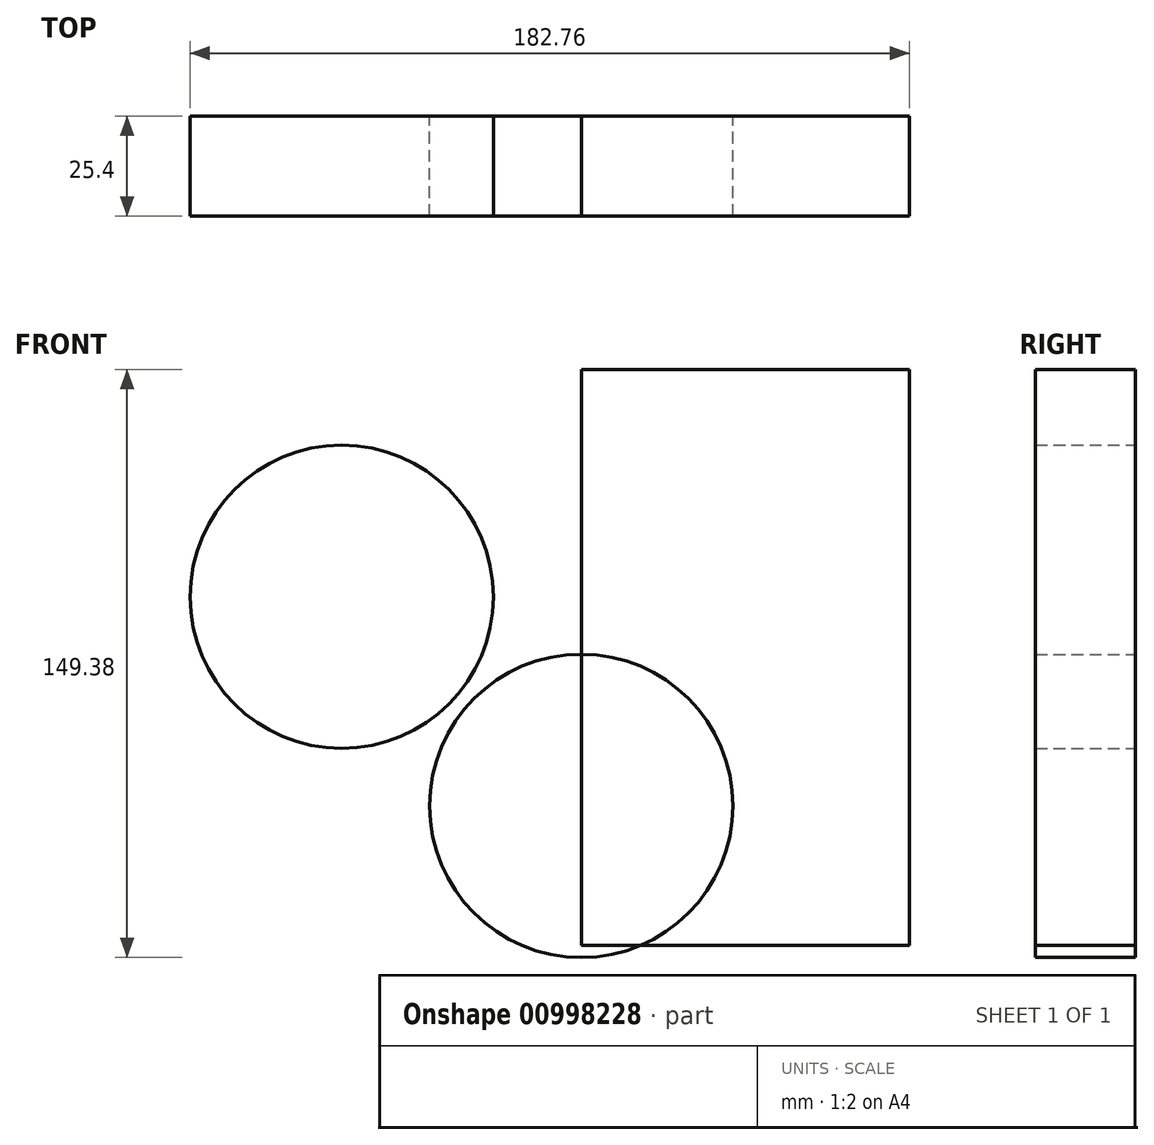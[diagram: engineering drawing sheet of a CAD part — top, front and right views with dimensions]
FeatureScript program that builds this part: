
annotation { "Feature Type Name" : "Feature", "Feature Type Description" : "" }
export const myFeature = defineFeature(function(context is Context, id is Id, definition is map)
    precondition{}
    {
        {
            var Q0;
            Q0=qCreatedBy(makeId("Front.planeOp"),FACE);
            var sketch = newSketch(context, id + "F0", { "sketchPlane" : qUnion([Q0])});
            skCircle(sketch, "E0", {"center": v(-60.87, 53.12) * mm, "radius": 38.52 * mm});
            skCircle(sketch, "E1", {"center": v(0, 0) * mm, "radius": 38.52 * mm});
            skSolve(sketch);
        }
        {
            var Q0;
            Q0 = qSketchRegion(id + "F0", true);
            extrude(context, id + "F1", {"entities" : qUnion([Q0]), "depth" : 25.4 * mm, "offsetDistance" : 25.4 * mm});
        }
        {
            var Q0;
            Q0=qCreatedBy(makeId("Front.planeOp"),FACE);
            var sketch = newSketch(context, id + "F2", { "sketchPlane" : qUnion([Q0])});
            skLineSegment(sketch, "E2.bottom", {"start": v(0, 110.86) * mm, "end": v(83.37, 110.86) * mm});
            skLineSegment(sketch, "E2.top", {"start": v(0, -35.47) * mm, "end": v(83.37, -35.47) * mm});
            skLineSegment(sketch, "E2.left", {"start": v(0, 110.86) * mm, "end": v(0, -35.47) * mm});
            skLineSegment(sketch, "E2.right", {"start": v(83.37, 110.86) * mm, "end": v(83.37, -35.47) * mm});
            skSolve(sketch);
        }
        {
            var Q0;
            Q0 = qSketchRegion(id + "F2", true);
            extrude(context, id + "F3", {"entities" : qUnion([Q0]), "depth" : 25.4 * mm, "offsetDistance" : 25.4 * mm});
        }
    });
